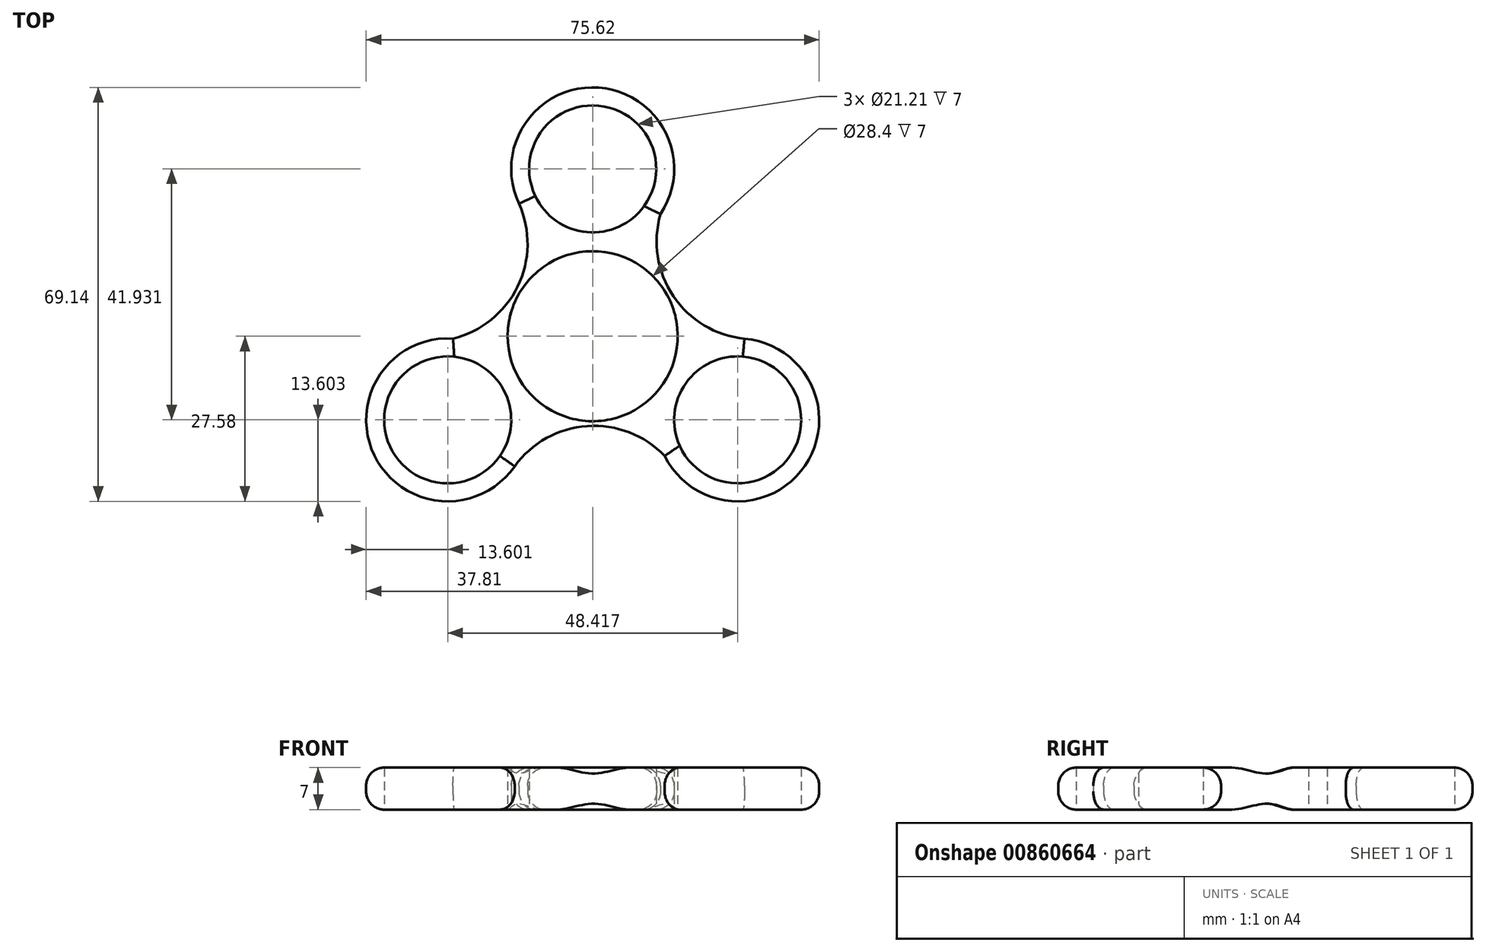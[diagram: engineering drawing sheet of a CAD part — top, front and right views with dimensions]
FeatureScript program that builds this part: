
annotation { "Feature Type Name" : "Feature", "Feature Type Description" : "" }
export const myFeature = defineFeature(function(context is Context, id is Id, definition is map)
    precondition{}
    {
        {
            var Q0;
            Q0=qCreatedBy(makeId("Top.planeOp"),FACE);
            var sketch = newSketch(context, id + "F0", { "sketchPlane" : qUnion([Q0])});
            skCircle(sketch, "E0", {"center": v(0, 0) * mm, "radius": 11.2 * mm});
            skCircle(sketch, "E1", {"center": v(0, 0) * mm, "radius": 14.2 * mm});
            skCircle(sketch, "E2", {"center": v(0, 27.95) * mm, "radius": 10.6 * mm});
            skCircle(sketch, "E3", {"center": v(0, 27.95) * mm, "radius": 13.6 * mm});
            skCircle(sketch, "E4.1.0", {"center": v(-24.2, -13.98) * mm, "radius": 10.6 * mm});
            skCircle(sketch, "E4.1.1", {"center": v(-24.2, -13.98) * mm, "radius": 13.6 * mm});
            skCircle(sketch, "E4.2.0", {"center": v(24.2, -13.98) * mm, "radius": 10.6 * mm});
            skCircle(sketch, "E4.2.1", {"center": v(24.2, -13.98) * mm, "radius": 13.6 * mm});
            skArc(sketch, "E5", {"start": v(-23.33, -0.4) * mm, "mid": v(-12.54, 8.3) * mm, "end": v(-12.3, 22.15) * mm});
            skArc(sketch, "E6.1.0", {"start": v(12.01, -20) * mm, "mid": v(-0.91, -15) * mm, "end": v(-13.03, -21.73) * mm});
            skArc(sketch, "E6.2.0", {"start": v(11.32, 20.4) * mm, "mid": v(13.45, 6.71) * mm, "end": v(25.34, -0.42) * mm});
            skSolve(sketch);
        }
        {
            var Q0;
            Q0 = qSketchRegion(id + "F0", true);
            extrude(context, id + "F1", {"entities" : qUnion([Q0]), "depth" : 7 * mm, "offsetDistance" : 25 * mm});
        }
        {
            var Q0;
            Q0=makeQuery(id+"F1.opExtrude","CAP_EDGE",EDGE,{"disambiguationData":[OSD([sQuery(id+"F0.wireOp",EDGE,"E5")])],"isStart":false});
            var Q1;
            Q1=makeQuery(id+"F1.opExtrude","CAP_EDGE",EDGE,{"disambiguationData":[OSD([sQuery(id+"F0.wireOp",EDGE,"E3")])],"isStart":false});
            var Q2;
            Q2=makeQuery(id+"F1.opExtrude","CAP_EDGE",EDGE,{"disambiguationData":[OSD([sQuery(id+"F0.wireOp",EDGE,"E4.1.1")])],"isStart":false});
            var Q3;
            Q3=makeQuery(id+"F1.opExtrude","CAP_EDGE",EDGE,{"disambiguationData":[OSD([sQuery(id+"F0.wireOp",EDGE,"E6.1.0")])],"isStart":false});
            var Q4;
            Q4=makeQuery(id+"F1.opExtrude","CAP_EDGE",EDGE,{"disambiguationData":[OSD([sQuery(id+"F0.wireOp",EDGE,"E4.2.1")])],"isStart":false});
            var Q5;
            Q5=makeQuery(id+"F1.opExtrude","CAP_EDGE",EDGE,{"disambiguationData":[OSD([sQuery(id+"F0.wireOp",EDGE,"E6.2.0")])],"isStart":false});
            fillet(context, id + "F2", {"entities" : qUnion([Q0, Q1, Q2, Q3, Q4, Q5]), "radius" : 3 * mm, "tangentPropagation" : true, "allowEdgeOverflow" : false});
        }
        {
            var Q0;
            Q0=makeQuery(id+"F1.opExtrude","CAP_EDGE",EDGE,{"disambiguationData":[OSD([sQuery(id+"F0.wireOp",EDGE,"E4.1.1")])],"isStart":true});
            var Q1;
            Q1=makeQuery(id+"F1.opExtrude","CAP_EDGE",EDGE,{"disambiguationData":[OSD([sQuery(id+"F0.wireOp",EDGE,"E4.2.1")])],"isStart":true});
            var Q2;
            Q2=makeQuery(id+"F1.opExtrude","CAP_EDGE",EDGE,{"disambiguationData":[OSD([sQuery(id+"F0.wireOp",EDGE,"E3")])],"isStart":true});
            var Q3;
            Q3=makeQuery(id+"F1.opExtrude","CAP_EDGE",EDGE,{"disambiguationData":[OSD([sQuery(id+"F0.wireOp",EDGE,"E6.2.0")])],"isStart":true});
            var Q4;
            Q4=makeQuery(id+"F1.opExtrude","CAP_EDGE",EDGE,{"disambiguationData":[OSD([sQuery(id+"F0.wireOp",EDGE,"E5")])],"isStart":true});
            var Q5;
            Q5=makeQuery(id+"F1.opExtrude","CAP_EDGE",EDGE,{"disambiguationData":[OSD([sQuery(id+"F0.wireOp",EDGE,"E6.1.0")])],"isStart":true});
            fillet(context, id + "F3", {"entities" : qUnion([Q0, Q1, Q2, Q3, Q4, Q5]), "radius" : 3 * mm, "tangentPropagation" : true, "allowEdgeOverflow" : false});
        }
    });
